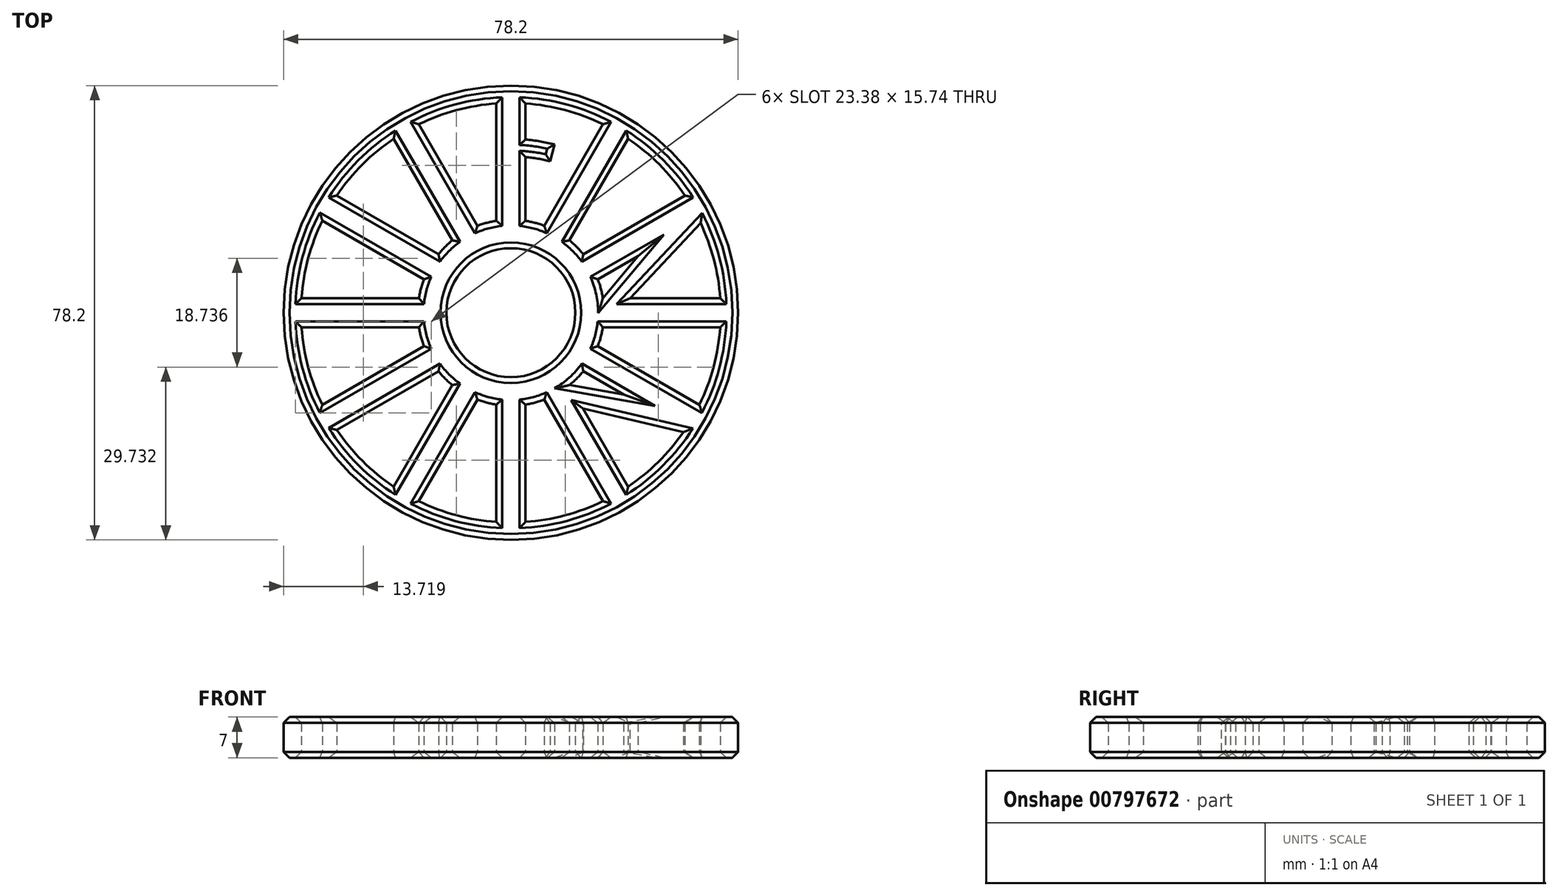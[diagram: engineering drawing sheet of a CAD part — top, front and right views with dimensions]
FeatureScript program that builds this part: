
annotation { "Feature Type Name" : "Feature", "Feature Type Description" : "" }
export const myFeature = defineFeature(function(context is Context, id is Id, definition is map)
    precondition{}
    {
        {
            var Q0;
            Q0=qCreatedBy(makeId("Top.planeOp"),FACE);
            var sketch = newSketch(context, id + "F0", { "sketchPlane" : qUnion([Q0])});
            skCircle(sketch, "E0", {"center": v(0, 0) * mm, "radius": 11.1 * mm});
            skCircle(sketch, "E1.cCircle", {"center": v(0, 0) * mm, "radius": 12.5 * mm, "construction": true});
            skLineSegment(sketch, "E1.0", {"start": v(21.65, -12.5) * mm, "end": v(-21.65, -12.5) * mm, "construction": true});
            skLineSegment(sketch, "E1.1", {"start": v(-21.65, -12.5) * mm, "end": v(0, 25) * mm, "construction": true});
            skLineSegment(sketch, "E1.2", {"start": v(0, 25) * mm, "end": v(21.65, -12.5) * mm, "construction": true});
            skPoint(sketch, "E1.0.midPoint", {"position": v(0, -12.5) * mm});
            skCircle(sketch, "E2", {"center": v(0, 25) * mm, "radius": 11.1 * mm});
            skLineSegment(sketch, "E3", {"start": v(0, 0) * mm, "end": v(-10.83, 6.25) * mm});
            skLineSegment(sketch, "E4", {"start": v(-10.83, 6.25) * mm, "end": v(10.83, 6.25) * mm, "construction": true});
            skLineSegment(sketch, "E5", {"start": v(10.83, 6.25) * mm, "end": v(0, 0) * mm});
            skLineSegment(sketch, "E6", {"start": v(0, -12.5) * mm, "end": v(0, 0) * mm, "construction": true});
            skLineSegment(sketch, "E7", {"start": v(10.83, 6.25) * mm, "end": v(0, -12.5) * mm, "construction": true});
            skLineSegment(sketch, "E8", {"start": v(-10.83, 6.25) * mm, "end": v(0, -12.5) * mm, "construction": true});
            skLineSegment(sketch, "E9", {"start": v(10.83, 6.25) * mm, "end": v(21.65, 12.5) * mm, "construction": true});
            skArc(sketch, "E10", {"start": v(12.21, 17.95) * mm, "mid": v(0, 39.1) * mm, "end": v(-12.21, 17.95) * mm});
            skArc(sketch, "E11", {"start": v(12.21, 7.05) * mm, "mid": v(10.75, 12.5) * mm, "end": v(12.21, 17.95) * mm});
            skArc(sketch, "E12.MirrorCS", {"start": v(-12.21, 7.05) * mm, "mid": v(-10.75, 12.5) * mm, "end": v(-12.21, 17.95) * mm});
            skCircle(sketch, "E13", {"center": v(0, 0) * mm, "radius": 14.1 * mm});
            skLineSegment(sketch, "E14", {"start": v(-10.83, 6.25) * mm, "end": v(-12.21, 7.05) * mm});
            skLineSegment(sketch, "E15", {"start": v(10.83, 6.25) * mm, "end": v(12.21, 7.05) * mm});
            skLineSegment(sketch, "E16", {"start": v(0, 0) * mm, "end": v(0, 39.1) * mm, "construction": true});
            skSolve(sketch);
        }
        {
            var Q0;
            Q0=qCreatedBy(makeId("Top.planeOp"),FACE);
            var sketch = newSketch(context, id + "F1", { "sketchPlane" : qUnion([Q0])});
            skCircle(sketch, "E17", {"center": v(0, 0) * mm, "radius": 39.1 * mm});
            skCircle(sketch, "E18", {"center": v(0, 0) * mm, "radius": 36.1 * mm});
            skCircle(sketch, "E19", {"center": v(0, 0) * mm, "radius": 16.02 * mm});
            skCircle(sketch, "E20", {"center": v(0, 0) * mm, "radius": 25 * mm, "construction": true});
            skLineSegment(sketch, "E21.bottom", {"start": v(-2.5, 15.82) * mm, "end": v(2.5, 15.82) * mm});
            skLineSegment(sketch, "E21.top", {"start": v(-2.5, 37.52) * mm, "end": v(2.5, 37.52) * mm});
            skLineSegment(sketch, "E21.left", {"start": v(-2.5, 15.82) * mm, "end": v(-2.5, 37.52) * mm});
            skLineSegment(sketch, "E21.right", {"start": v(2.5, 15.82) * mm, "end": v(2.5, 37.52) * mm});
            skPoint(sketch, "E21.middle", {"position": v(0, 26.67) * mm});
            skPoint(sketch, "E22.middle", {"position": v(15.01, 20) * mm});
            skSolve(sketch);
        }
        {
            var Q0;
            {var subQ0=sQuery(id+"F1.wireOp",EDGE,"E21.left");var subQ1=sQuery(id+"F1.wireOp",EDGE,"E18");var subQ2=makeQuery(id+"F1.imprint","INTERSECT",VERTEX,{"derivedFrom":[subQ1,subQ0]});Q0=makeQuery(id+"F1.imprint","IMPRINT",FACE,{"disambiguationData":[TD([[makeQuery(id+"F1.imprint","IMPRINT",EDGE,{"disambiguationData":[TD([[subQ2,1.0]])],"derivedFrom":subQ1}),1.0]])]});}
            var Q1;
            {var subQ5=sQuery(id+"F1.wireOp",EDGE,"E21.top");Q1=makeQuery(id+"F1.imprint","IMPRINT",FACE,{"disambiguationData":[TD([[makeQuery(id+"F1.imprint","IMPRINT",EDGE,{"derivedFrom":subQ5}),-1.0]])]});}
            var Q2;
            {var subQ5=sQuery(id+"F1.wireOp",EDGE,"E21.bottom");Q2=makeQuery(id+"F1.imprint","IMPRINT",FACE,{"disambiguationData":[TD([[makeQuery(id+"F1.imprint","IMPRINT",EDGE,{"derivedFrom":subQ5}),1.0]])]});}
            extrude(context, id + "F2", {"entities" : qUnion([Q0, Q1, Q2]), "depth" : 7 * mm, "offsetDistance" : 25 * mm});
        }
        {
            var Q0;
            Q0=makeQuery(id+"F2.opExtrude","SWEPT_BODY",BODY,{"disambiguationData":[OSD([sQuery(id+"F1.wireOp",EDGE,"E21.bottom"),sQuery(id+"F1.wireOp",EDGE,"E21.top"),sQuery(id+"F1.wireOp",EDGE,"E21.left"),sQuery(id+"F1.wireOp",EDGE,"E21.right")])]});
            var Q1;
            Q1=sQuery(id+"F0.wireOp",EDGE,"E0");
            circularPattern(context, id + "F3", {"entities" : qUnion([Q0]), "axis" : qUnion([Q1]), "angle" : 360 * degree, "instanceCount" : 12, "equalSpace" : true});
        }
        {
            var Q0;
            Q0=qCreatedBy(makeId("Top.planeOp"),FACE);
            var sketch = newSketch(context, id + "F4", { "sketchPlane" : qUnion([Q0])});
            skArc(sketch, "E23", {"start": v(0, 29.92) * mm, "mid": v(3.77, 29.68) * mm, "end": v(7.49, 28.96) * mm});
            skArc(sketch, "E24", {"start": v(0, 26.92) * mm, "mid": v(3.4, 26.7) * mm, "end": v(6.73, 26.06) * mm});
            skLineSegment(sketch, "E25", {"start": v(7.49, 28.96) * mm, "end": v(6.73, 26.06) * mm});
            skLineSegment(sketch, "E26", {"start": v(0, 29.92) * mm, "end": v(0, 26.92) * mm});
            skLineSegment(sketch, "E27", {"start": v(31.24, 20.93) * mm, "end": v(15.82, 2.5) * mm});
            skLineSegment(sketch, "E28", {"start": v(15.82, 2.5) * mm, "end": v(15.82, -2.5) * mm});
            skLineSegment(sketch, "E29", {"start": v(15.82, -2.5) * mm, "end": v(33.74, 16.6) * mm});
            skLineSegment(sketch, "E30", {"start": v(33.74, 16.6) * mm, "end": v(31.24, 20.93) * mm});
            skLineSegment(sketch, "E31", {"start": v(33.74, -16.6) * mm, "end": v(10.08, -12.45) * mm});
            skLineSegment(sketch, "E32", {"start": v(10.08, -12.45) * mm, "end": v(5.75, -14.95) * mm});
            skLineSegment(sketch, "E33", {"start": v(5.75, -14.95) * mm, "end": v(31.24, -20.93) * mm});
            skLineSegment(sketch, "E34", {"start": v(31.24, -20.93) * mm, "end": v(33.74, -16.6) * mm});
            skSolve(sketch);
        }
        {
            var Q0;
            Q0 = qSketchRegion(id + "F4", true);
            extrude(context, id + "F5", {"entities" : qUnion([Q0]), "operationType" : NewBodyOperationType.ADD, "depth" : 7 * mm, "offsetDistance" : 25 * mm});
        }
        {
            var Q0;
            Q0=makeQuery(id+"F1.imprint","IMPRINT",FACE,{"disambiguationData":[TD([[makeQuery(id+"F1.imprint","IMPRINT",EDGE,{"derivedFrom":sQuery(id+"F1.wireOp",EDGE,"E17")}),1.0]])]});
            var Q1;
            {var subQ5=sQuery(id+"F1.wireOp",EDGE,"E21.top");Q1=makeQuery(id+"F1.imprint","IMPRINT",FACE,{"disambiguationData":[TD([[makeQuery(id+"F1.imprint","IMPRINT",EDGE,{"derivedFrom":subQ5}),-1.0]])]});}
            extrude(context, id + "F6", {"entities" : qUnion([Q0, Q1]), "operationType" : NewBodyOperationType.ADD, "depth" : 7 * mm, "offsetDistance" : 25 * mm});
        }
        {
            var Q0;
            {var subQ2=sQuery(id+"F0.wireOp",EDGE,"E14");Q0=makeQuery(id+"F0.imprint","IMPRINT",FACE,{"disambiguationData":[TD([[makeQuery(id+"F0.imprint","IMPRINT",EDGE,{"derivedFrom":subQ2}),1.0]])]});}
            var Q1;
            {var subQ0=sQuery(id+"F1.wireOp",EDGE,"E21.bottom");Q1=makeQuery(id+"F1.imprint","IMPRINT",FACE,{"disambiguationData":[TD([[makeQuery(id+"F1.imprint","IMPRINT",EDGE,{"derivedFrom":subQ0}),-1.0]])]});}
            extrude(context, id + "F7", {"entities" : qUnion([Q0, Q1]), "operationType" : NewBodyOperationType.ADD, "depth" : 7 * mm, "offsetDistance" : 25 * mm});
        }
        {
            var Q0;
            {var subQ0=sQuery(id+"F0.wireOp",EDGE,"E3");var subQ1=sQuery(id+"F0.wireOp",EDGE,"E0");var subQ2=makeQuery(id+"F0.imprint","INTERSECT",VERTEX,{"derivedFrom":[subQ1,subQ0]});Q0=makeQuery(id+"F0.imprint","IMPRINT",FACE,{"disambiguationData":[TD([[makeQuery(id+"F0.imprint","IMPRINT",EDGE,{"disambiguationData":[TD([[subQ2,-1.0]])],"derivedFrom":subQ1}),1.0]])]});}
            var Q1;
            {var subQ0=sQuery(id+"F0.wireOp",EDGE,"E3");var subQ1=sQuery(id+"F0.wireOp",EDGE,"E0");var subQ2=makeQuery(id+"F0.imprint","INTERSECT",VERTEX,{"derivedFrom":[subQ1,subQ0]});Q1=makeQuery(id+"F0.imprint","IMPRINT",FACE,{"disambiguationData":[TD([[makeQuery(id+"F0.imprint","IMPRINT",EDGE,{"disambiguationData":[TD([[subQ2,1.0]])],"derivedFrom":subQ1}),1.0]])]});}
            extrude(context, id + "F8", {"entities" : qUnion([Q0, Q1]), "operationType" : NewBodyOperationType.REMOVE, "depth" : 25 * mm, "offsetDistance" : 25 * mm});
        }
        {
            var Q0;
            {var subQ0=sQuery(id+"F1.wireOp",EDGE,"E21.bottom");var subQ1=sQuery(id+"F4.wireOp",EDGE,"E26");var subQ2=sQuery(id+"F4.wireOp",EDGE,"E25");var subQ3=sQuery(id+"F4.wireOp",EDGE,"E24");var subQ4=sQuery(id+"F4.wireOp",EDGE,"E23");var subQ5=makeQuery(id+"F2.opExtrude","CAP_FACE",FACE,{"disambiguationData":[OSD([subQ0,sQuery(id+"F1.wireOp",EDGE,"E21.top"),sQuery(id+"F1.wireOp",EDGE,"E21.left"),sQuery(id+"F1.wireOp",EDGE,"E21.right")])],"isStart":false});var subQ6=sQuery(id+"F4.wireOp",EDGE,"E30");var subQ7=sQuery(id+"F4.wireOp",EDGE,"E29");var subQ8=sQuery(id+"F4.wireOp",EDGE,"E28");var subQ9=sQuery(id+"F4.wireOp",EDGE,"E27");var subQ10=sQuery(id+"F4.wireOp",EDGE,"E34");var subQ11=sQuery(id+"F4.wireOp",EDGE,"E33");var subQ12=sQuery(id+"F4.wireOp",EDGE,"E32");var subQ13=sQuery(id+"F4.wireOp",EDGE,"E31");Q0=makeQuery(id+"F7.boolean.opBoolean","MERGE",FACE,{"derivedFrom":[makeQuery(id+"F6.boolean.opBoolean","MERGE",FACE,{"derivedFrom":[makeQuery(id+"F3.opPattern","COPY",FACE,{"derivedFrom":subQ5,"instanceName":"5"}),makeQuery(id+"F3.opPattern","COPY",FACE,{"derivedFrom":subQ5,"instanceName":"11"}),makeQuery(id+"F5.boolean.opBoolean","MERGE",FACE,{"derivedFrom":[subQ5,makeQuery(id+"F5.opExtrude","CAP_FACE",FACE,{"disambiguationData":[OSD([subQ4,subQ3,subQ2,subQ1])],"isStart":false})]}),makeQuery(id+"F5.boolean.opBoolean","MERGE",FACE,{"derivedFrom":[makeQuery(id+"F3.opPattern","COPY",FACE,{"derivedFrom":subQ5,"instanceName":"7"}),makeQuery(id+"F3.opPattern","COPY",FACE,{"derivedFrom":subQ5,"instanceName":"8"}),makeQuery(id+"F5.opExtrude","CAP_FACE",FACE,{"disambiguationData":[OSD([subQ13,subQ12,subQ11,subQ10])],"isStart":false})]}),makeQuery(id+"F5.boolean.opBoolean","MERGE",FACE,{"derivedFrom":[makeQuery(id+"F3.opPattern","COPY",FACE,{"derivedFrom":subQ5,"instanceName":"9"}),makeQuery(id+"F3.opPattern","COPY",FACE,{"derivedFrom":subQ5,"instanceName":"10"}),makeQuery(id+"F5.opExtrude","CAP_FACE",FACE,{"disambiguationData":[OSD([subQ9,subQ8,subQ7,subQ6])],"isStart":false})]}),makeQuery(id+"FkwK2uHwcBlUYSS_1.1.F5.boolean.opBoolean","MERGE",FACE,{"derivedFrom":[makeQuery(id+"F3.opPattern","COPY",FACE,{"derivedFrom":subQ5,"instanceName":"1"}),makeQuery(id+"F3.opPattern","COPY",FACE,{"derivedFrom":subQ5,"instanceName":"2"}),makeQuery(id+"FkwK2uHwcBlUYSS_1.1.F5.opExtrude","CAP_FACE",FACE,{"disambiguationData":[OSD([subQ13,subQ12,subQ11,subQ10])],"isStart":false})]}),makeQuery(id+"FkwK2uHwcBlUYSS_1.1.F5.boolean.opBoolean","MERGE",FACE,{"derivedFrom":[makeQuery(id+"F3.opPattern","COPY",FACE,{"derivedFrom":subQ5,"instanceName":"3"}),makeQuery(id+"F3.opPattern","COPY",FACE,{"derivedFrom":subQ5,"instanceName":"4"}),makeQuery(id+"FkwK2uHwcBlUYSS_1.1.F5.opExtrude","CAP_FACE",FACE,{"disambiguationData":[OSD([subQ9,subQ8,subQ7,subQ6])],"isStart":false})]}),makeQuery(id+"FkwK2uHwcBlUYSS_1.1.F5.boolean.opBoolean","MERGE",FACE,{"derivedFrom":[makeQuery(id+"F3.opPattern","COPY",FACE,{"derivedFrom":subQ5,"instanceName":"6"}),makeQuery(id+"FkwK2uHwcBlUYSS_1.1.F5.opExtrude","CAP_FACE",FACE,{"disambiguationData":[OSD([subQ4,subQ3,subQ2,subQ1])],"isStart":false})]}),makeQuery(id+"F6.opExtrude","CAP_FACE",FACE,{"disambiguationData":[OSD([sQuery(id+"F1.wireOp",EDGE,"E17"),sQuery(id+"F1.wireOp",EDGE,"E18")])],"isStart":false})]}),makeQuery(id+"F7.opExtrude","CAP_FACE",FACE,{"disambiguationData":[OSD([sQuery(id+"F0.wireOp",EDGE,"E0"),sQuery(id+"F0.wireOp",EDGE,"E3"),sQuery(id+"F0.wireOp",EDGE,"E5"),sQuery(id+"F0.wireOp",EDGE,"E13"),sQuery(id+"F0.wireOp",EDGE,"E14"),sQuery(id+"F0.wireOp",EDGE,"E15")])],"isStart":false}),makeQuery(id+"F7.opExtrude","CAP_FACE",FACE,{"disambiguationData":[OSD([sQuery(id+"F1.wireOp",EDGE,"E19"),subQ0])],"isStart":false})]});}
            var Q1;
            {var subQ0=sQuery(id+"F1.wireOp",EDGE,"E21.bottom");var subQ1=sQuery(id+"F4.wireOp",EDGE,"E26");var subQ2=sQuery(id+"F4.wireOp",EDGE,"E25");var subQ3=sQuery(id+"F4.wireOp",EDGE,"E24");var subQ4=sQuery(id+"F4.wireOp",EDGE,"E23");var subQ5=makeQuery(id+"F2.opExtrude","CAP_FACE",FACE,{"disambiguationData":[OSD([subQ0,sQuery(id+"F1.wireOp",EDGE,"E21.top"),sQuery(id+"F1.wireOp",EDGE,"E21.left"),sQuery(id+"F1.wireOp",EDGE,"E21.right")])],"isStart":true});var subQ6=sQuery(id+"F4.wireOp",EDGE,"E30");var subQ7=sQuery(id+"F4.wireOp",EDGE,"E29");var subQ8=sQuery(id+"F4.wireOp",EDGE,"E28");var subQ9=sQuery(id+"F4.wireOp",EDGE,"E27");var subQ10=sQuery(id+"F4.wireOp",EDGE,"E34");var subQ11=sQuery(id+"F4.wireOp",EDGE,"E33");var subQ12=sQuery(id+"F4.wireOp",EDGE,"E32");var subQ13=sQuery(id+"F4.wireOp",EDGE,"E31");Q1=makeQuery(id+"F7.boolean.opBoolean","MERGE",FACE,{"derivedFrom":[makeQuery(id+"F6.boolean.opBoolean","MERGE",FACE,{"derivedFrom":[makeQuery(id+"F3.opPattern","COPY",FACE,{"derivedFrom":subQ5,"instanceName":"5"}),makeQuery(id+"F3.opPattern","COPY",FACE,{"derivedFrom":subQ5,"instanceName":"11"}),makeQuery(id+"F5.boolean.opBoolean","MERGE",FACE,{"derivedFrom":[subQ5,makeQuery(id+"F5.opExtrude","CAP_FACE",FACE,{"disambiguationData":[OSD([subQ4,subQ3,subQ2,subQ1])],"isStart":true})]}),makeQuery(id+"F5.boolean.opBoolean","MERGE",FACE,{"derivedFrom":[makeQuery(id+"F3.opPattern","COPY",FACE,{"derivedFrom":subQ5,"instanceName":"7"}),makeQuery(id+"F3.opPattern","COPY",FACE,{"derivedFrom":subQ5,"instanceName":"8"}),makeQuery(id+"F5.opExtrude","CAP_FACE",FACE,{"disambiguationData":[OSD([subQ13,subQ12,subQ11,subQ10])],"isStart":true})]}),makeQuery(id+"F5.boolean.opBoolean","MERGE",FACE,{"derivedFrom":[makeQuery(id+"F3.opPattern","COPY",FACE,{"derivedFrom":subQ5,"instanceName":"9"}),makeQuery(id+"F3.opPattern","COPY",FACE,{"derivedFrom":subQ5,"instanceName":"10"}),makeQuery(id+"F5.opExtrude","CAP_FACE",FACE,{"disambiguationData":[OSD([subQ9,subQ8,subQ7,subQ6])],"isStart":true})]}),makeQuery(id+"FkwK2uHwcBlUYSS_1.1.F5.boolean.opBoolean","MERGE",FACE,{"derivedFrom":[makeQuery(id+"F3.opPattern","COPY",FACE,{"derivedFrom":subQ5,"instanceName":"1"}),makeQuery(id+"F3.opPattern","COPY",FACE,{"derivedFrom":subQ5,"instanceName":"2"}),makeQuery(id+"FkwK2uHwcBlUYSS_1.1.F5.opExtrude","CAP_FACE",FACE,{"disambiguationData":[OSD([subQ13,subQ12,subQ11,subQ10])],"isStart":true})]}),makeQuery(id+"FkwK2uHwcBlUYSS_1.1.F5.boolean.opBoolean","MERGE",FACE,{"derivedFrom":[makeQuery(id+"F3.opPattern","COPY",FACE,{"derivedFrom":subQ5,"instanceName":"3"}),makeQuery(id+"F3.opPattern","COPY",FACE,{"derivedFrom":subQ5,"instanceName":"4"}),makeQuery(id+"FkwK2uHwcBlUYSS_1.1.F5.opExtrude","CAP_FACE",FACE,{"disambiguationData":[OSD([subQ9,subQ8,subQ7,subQ6])],"isStart":true})]}),makeQuery(id+"FkwK2uHwcBlUYSS_1.1.F5.boolean.opBoolean","MERGE",FACE,{"derivedFrom":[makeQuery(id+"F3.opPattern","COPY",FACE,{"derivedFrom":subQ5,"instanceName":"6"}),makeQuery(id+"FkwK2uHwcBlUYSS_1.1.F5.opExtrude","CAP_FACE",FACE,{"disambiguationData":[OSD([subQ4,subQ3,subQ2,subQ1])],"isStart":true})]}),makeQuery(id+"F6.opExtrude","CAP_FACE",FACE,{"disambiguationData":[OSD([sQuery(id+"F1.wireOp",EDGE,"E17"),sQuery(id+"F1.wireOp",EDGE,"E18")])],"isStart":true})]}),makeQuery(id+"F7.opExtrude","CAP_FACE",FACE,{"disambiguationData":[OSD([sQuery(id+"F0.wireOp",EDGE,"E0"),sQuery(id+"F0.wireOp",EDGE,"E3"),sQuery(id+"F0.wireOp",EDGE,"E5"),sQuery(id+"F0.wireOp",EDGE,"E13"),sQuery(id+"F0.wireOp",EDGE,"E14"),sQuery(id+"F0.wireOp",EDGE,"E15")])],"isStart":true}),makeQuery(id+"F7.opExtrude","CAP_FACE",FACE,{"disambiguationData":[OSD([sQuery(id+"F1.wireOp",EDGE,"E19"),subQ0])],"isStart":true})]});}
            chamfer(context, id + "F9", {"entities" : qUnion([Q0, Q1]), "width" : 1 * mm, "tangentPropagation" : true});
        }
    });
